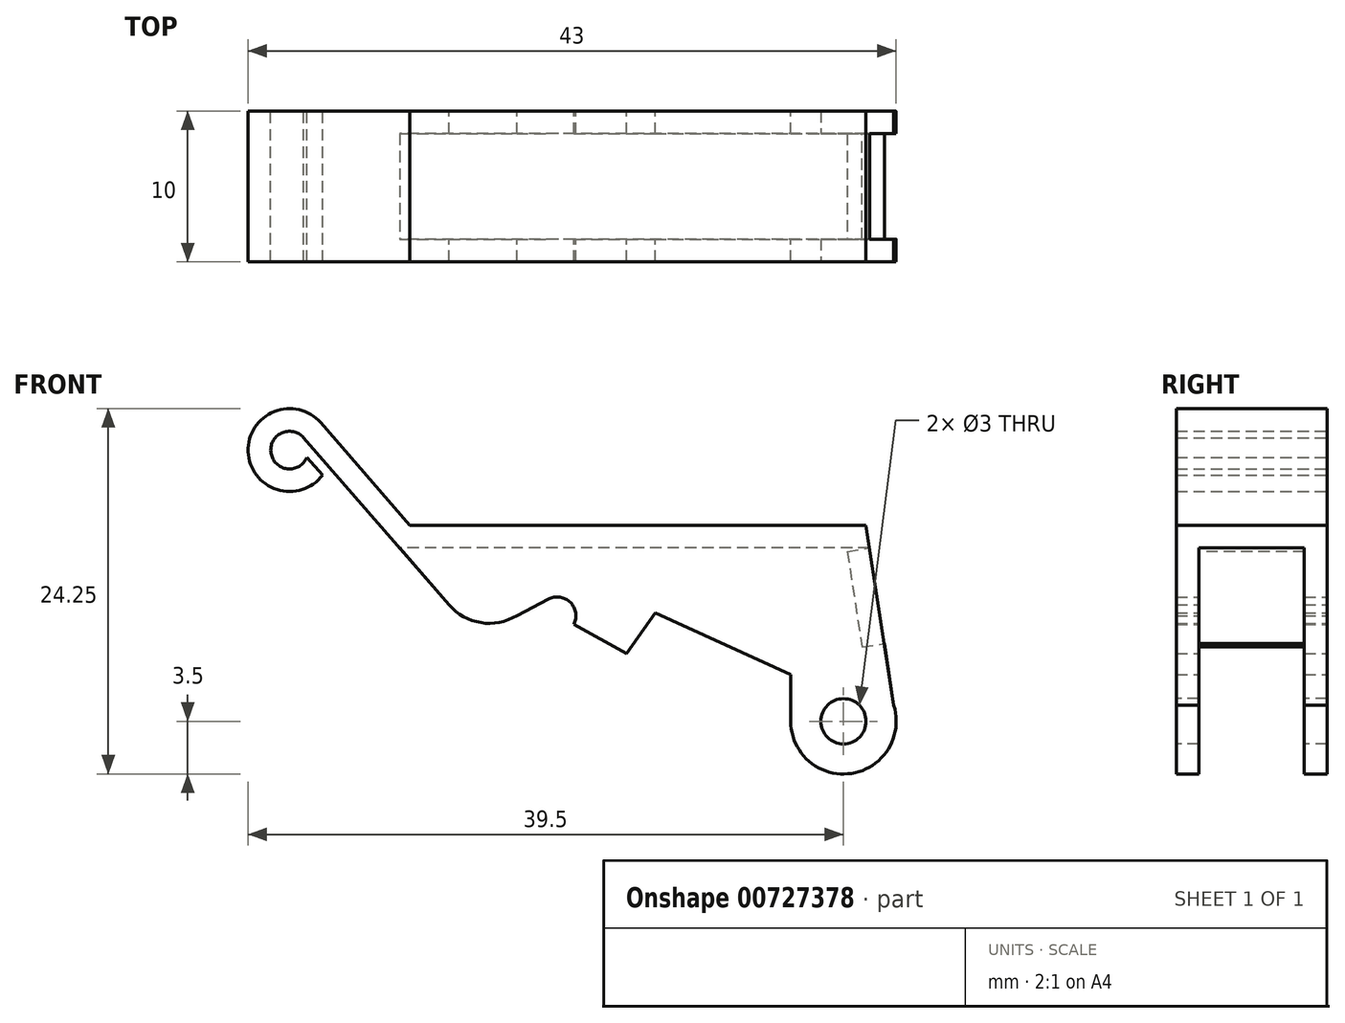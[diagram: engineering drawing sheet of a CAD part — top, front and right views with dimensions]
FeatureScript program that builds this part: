
annotation { "Feature Type Name" : "Feature", "Feature Type Description" : "" }
export const myFeature = defineFeature(function(context is Context, id is Id, definition is map)
    precondition{}
    {
        {
            var Q0;
            Q0=qCreatedBy(makeId("Front.planeOp"),FACE);
            var sketch = newSketch(context, id + "F0", { "sketchPlane" : qUnion([Q0])});
            skArc(sketch, "E0", {"start": v(-3.5, 0) * mm, "mid": v(0.53, -3.46) * mm, "end": v(3.34, 1.05) * mm});
            skArc(sketch, "E1", {"start": v(-34.69, 19.82) * mm, "mid": v(-39.5, 17.9) * mm, "end": v(-34.56, 16.33) * mm});
            skLineSegment(sketch, "E2", {"start": v(-36.75, 18) * mm, "end": v(-39.5, 18) * mm, "construction": true});
            skLineSegment(sketch, "E3", {"start": v(-39.5, 18) * mm, "end": v(-39.5, -19.3) * mm, "construction": true});
            skLineSegment(sketch, "E4", {"start": v(0, 0) * mm, "end": v(3.5, 0) * mm, "construction": true});
            skLineSegment(sketch, "E5", {"start": v(3.5, 0) * mm, "end": v(3.5, -13.19) * mm, "construction": true});
            skLineSegment(sketch, "E6", {"start": v(-35.5, 18) * mm, "end": v(30.25, 18) * mm, "construction": true});
            skLineSegment(sketch, "E7", {"start": v(-34.69, 19.82) * mm, "end": v(-28.76, 13) * mm});
            skLineSegment(sketch, "E8", {"start": v(-28.76, 13) * mm, "end": v(1.5, 13) * mm});
            skLineSegment(sketch, "E9", {"start": v(1.5, 13) * mm, "end": v(3.5, 0) * mm});
            skLineSegment(sketch, "E10", {"start": v(3.5, 0) * mm, "end": v(3.5, 33.25) * mm, "construction": true});
            skArc(sketch, "E11", {"start": v(-35.82, 18.83) * mm, "mid": v(-37.98, 17.8) * mm, "end": v(-35.6, 17.52) * mm});
            skLineSegment(sketch, "E12", {"start": v(-35.82, 18.83) * mm, "end": v(-26.1, 7.67) * mm});
            skLineSegment(sketch, "E13", {"start": v(-3.5, 3.11) * mm, "end": v(-3.5, 0) * mm});
            skLineSegment(sketch, "E14", {"start": v(-35.6, 17.52) * mm, "end": v(-34.56, 16.33) * mm});
            skArc(sketch, "E15", {"start": v(-26.17, 7.74) * mm, "mid": v(-24.06, 6.54) * mm, "end": v(-21.67, 7.02) * mm});
            skArc(sketch, "E16", {"start": v(-17.89, 6.43) * mm, "mid": v(-18.12, 7.89) * mm, "end": v(-19.58, 8.1) * mm});
            skLineSegment(sketch, "E17", {"start": v(-21.67, 7.02) * mm, "end": v(-19.58, 8.1) * mm});
            skLineSegment(sketch, "E18", {"start": v(-17.89, 6.43) * mm, "end": v(-14.38, 4.5) * mm});
            skLineSegment(sketch, "E19", {"start": v(-14.38, 4.5) * mm, "end": v(-12.5, 7.2) * mm});
            skLineSegment(sketch, "E20", {"start": v(-12.5, 7.2) * mm, "end": v(-3.5, 3.11) * mm});
            skSolve(sketch);
        }
        {
            var Q0;
            Q0=qSketchRegion(id+"F0",true);
            extrude(context, id + "F1", {"entities" : qUnion([Q0]), "depth" : 10 * mm, "offsetDistance" : 25 * mm});
        }
        {
            var Q0;
            Q0=qCreatedBy(makeId("Top.planeOp"),FACE);
            cPlane(context, id + "F2", {"entities" : qUnion([Q0]), "cplaneType" : CPlaneType.OFFSET, "offset" : 5 * mm, "oppositeDirection" : true, "width" : 150 * mm, "height" : 150 * mm});
        }
        {
            var Q0;
            Q0=qCreatedBy(id+"F2.planeOp",FACE);
            var sketch = newSketch(context, id + "F3", { "sketchPlane" : qUnion([Q0])});
            skLineSegment(sketch, "E21", {"start": v(-5.38, -4.8) * mm, "end": v(-19.68, -4.8) * mm, "construction": true});
            skLineSegment(sketch, "E22", {"start": v(6.5, -8.5) * mm, "end": v(-37.24, -8.5) * mm});
            skLineSegment(sketch, "E23", {"start": v(6.3, -1.5) * mm, "end": v(-37.67, -1.5) * mm});
            skLineSegment(sketch, "E24", {"start": v(6.5, -8.5) * mm, "end": v(6.3, -1.5) * mm});
            skLineSegment(sketch, "E25", {"start": v(-37.24, -8.5) * mm, "end": v(-37.67, -1.5) * mm});
            skSolve(sketch);
        }
        {
            var Q0;
            Q0=qSketchRegion(id+"F3",true);
            extrude(context, id + "F4", {"entities" : qUnion([Q0]), "operationType" : NewBodyOperationType.REMOVE, "depth" : 16.5 * mm, "offsetDistance" : 25 * mm});
        }
        {
            var Q0;
            Q0=makeQuery(id+"F1.opExtrude","SWEPT_FACE",FACE,{"disambiguationData":[OSD([sQuery(id+"F0.wireOp",EDGE,"E9")])]});
            var sketch = newSketch(context, id + "F5", { "sketchPlane" : qUnion([Q0])});
            skPoint(sketch, "E26", {"position": v(-5, 12.62) * mm});
            skPoint(sketch, "E27", {"position": v(-5, 11.1) * mm});
            skSolve(sketch);
        }
        {
            var Q0;
            {var subQ2=sQuery(id+"F0.wireOp",EDGE,"E9");Q0=makeQuery(id+"F5.imprint","IMPRINT",FACE,{"disambiguationData":[TD([[makeQuery(id+"F5.imprint","IMPRINT",EDGE,{"derivedFrom":makeQuery(id+"F1.opExtrude","CAP_EDGE",EDGE,{"disambiguationData":[OSD([subQ2])],"isStart":true})}),-1.0]])]});}
            var sketch = newSketch(context, id + "F6", { "sketchPlane" : qUnion([Q0])});
            skLineSegment(sketch, "E28", {"start": v(-8.5, 4.68) * mm, "end": v(-1.5, 4.68) * mm});
            skLineSegment(sketch, "E29", {"start": v(-1.5, 4.68) * mm, "end": v(-1.5, 11.1) * mm});
            skLineSegment(sketch, "E30", {"start": v(-1.5, 11.1) * mm, "end": v(-8.5, 11.1) * mm});
            skLineSegment(sketch, "E31", {"start": v(-8.5, 11.1) * mm, "end": v(-8.5, 4.68) * mm});
            skSolve(sketch);
        }
        {
            var Q0;
            Q0=qSketchRegion(id+"F6",true);
            extrude(context, id + "F7", {"entities" : qUnion([Q0]), "oppositeDirection" : true, "depth" : 1.5 * mm, "offsetDistance" : 25 * mm});
        }
        {
            var Q0;
            Q0=makeQuery(id+"F1.opExtrude","CAP_FACE",FACE,{"disambiguationData":[OSD([sQuery(id+"F0.wireOp",EDGE,"E0"),sQuery(id+"F0.wireOp",EDGE,"E1"),sQuery(id+"F0.wireOp",EDGE,"E7"),sQuery(id+"F0.wireOp",EDGE,"E8"),sQuery(id+"F0.wireOp",EDGE,"E9"),sQuery(id+"F0.wireOp",EDGE,"E11"),sQuery(id+"F0.wireOp",EDGE,"E12"),sQuery(id+"F0.wireOp",EDGE,"E13"),sQuery(id+"F0.wireOp",EDGE,"E14"),sQuery(id+"F0.wireOp",EDGE,"E15"),sQuery(id+"F0.wireOp",EDGE,"E16"),sQuery(id+"F0.wireOp",EDGE,"E17"),sQuery(id+"F0.wireOp",EDGE,"E18"),sQuery(id+"F0.wireOp",EDGE,"E19"),sQuery(id+"F0.wireOp",EDGE,"E20")])],"isStart":false});
            var sketch = newSketch(context, id + "F8", { "sketchPlane" : qUnion([Q0])});
            skCircle(sketch, "E32", {"center": v(0, 0) * mm, "radius": 1.5 * mm});
            skSolve(sketch);
        }
        {
            var Q0;
            Q0=qSketchRegion(id+"F8",true);
            extrude(context, id + "F9", {"entities" : qUnion([Q0]), "operationType" : NewBodyOperationType.REMOVE, "endBound" : BoundingType.THROUGH_ALL, "oppositeDirection" : true, "depth" : 25 * mm, "offsetDistance" : 25 * mm});
        }
    });
